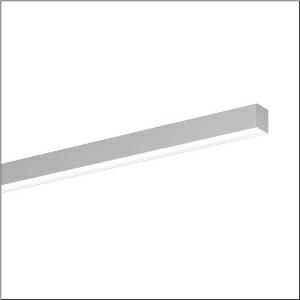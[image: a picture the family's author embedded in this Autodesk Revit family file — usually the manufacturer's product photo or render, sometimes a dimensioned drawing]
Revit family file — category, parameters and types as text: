
# Revit family: silica_r__21_51mx23dc3asb_5b95
name_source: partatom
category: Lighting Fixtures
units: mm (PartAtom-declared; Revit-internal decimal feet)

## family parameters
Cut with Voids When Loaded = No
Host = Face
Light Source = No
Part Type = Normal
Room Calculation Point = No
Round Connector Dimension = Use Diameter
Shared = No

## types (1)
- --- (1 x LED, 8200 lm, 62.2 W, 3000K)
    Apparent Load = 62 VA
    CIE Flux Codes = 78 96 99 100 100
    Color Rendering = 80
    Color Temperature = 3000K
    Default Elevation = 1800 mm
    Description = Silica® 21, office luminaire, primary optical cover: prismatic diffuser, of PMMA, CAT 2 (L<= 3000cd/m²), light emission: direct distribution, primary light characteristic: symmetric, installation type: surface-mounted, LED, rated luminous flux: 8.200lm, luminous efficacy: 132lm/W, light colour: 830, colour temperature: 3000K, control gear: DALI 2, with terminal, 3+2-pole, max. 2.5mm², mains connection: 220..240V, AC, 50/60Hz, rated input power: 62.2W, luminaire housing, of aluminium, metallic grey (RAL 9006), length: 3.004mm, width: 53mm, height: 53mm, protection rating (complete): IP20, insulation class (complete): insulation class I (protective earthing), certification: CE, permissible operating ambient temperature: 0..+35°C, standard: EN 50419, packaging unit: 1 piece
    Height = 53 mm
    Lamp = 1 x LED
    Lamp Light Flux = 8200 lm
    Lamp Power = 62.2 W
    Lamp count = 1
    Length = 3004 mm
    Luminous efficacy = 132 lm/W
    Manufacturer = Siteco
    ModVariant = No
    Model = 51MX23DC3ASB
    Mounting Place = Ceiling
    Mounting Type = Surface mounted
    Number of Poles = 1
    OnlyDefault = Yes
    Power Factor = 1
    Product Name = Silica® 21
    Product group = office luminaire | ceiling mounted
    ProductGroupID = 302
    Protection Class = Protection class I
    Protection Degree = IP 20
    RLX_Detail_Level = 1
    RLX_Emergency_Light_Flux = 0 lm
    RLX_Emergency_Type = 0
    RLX_Emergency_Type_DB = No
    RlxData = <blob elided: 21205 chars, md5=8877dcbd>
    Socket = socket
    Standby Power = 0 W
    System Light Flux = 8200 lm
    System Power = 62 W
    Type Comments = factory setting: luminous flux: 100 % | dim-lin: 254 | 345 mA
    Type Image = l_1335933.jpg
    URL = http://relux.com
    VarID = @adj_119128
    Voltage = 0 V
    Weight = 0.00 kg
    Width = 53 mm

## geometry (parser evidence)
native form markers: Blend x4, Sweep x11
no freeform markers — native parametric forms only
